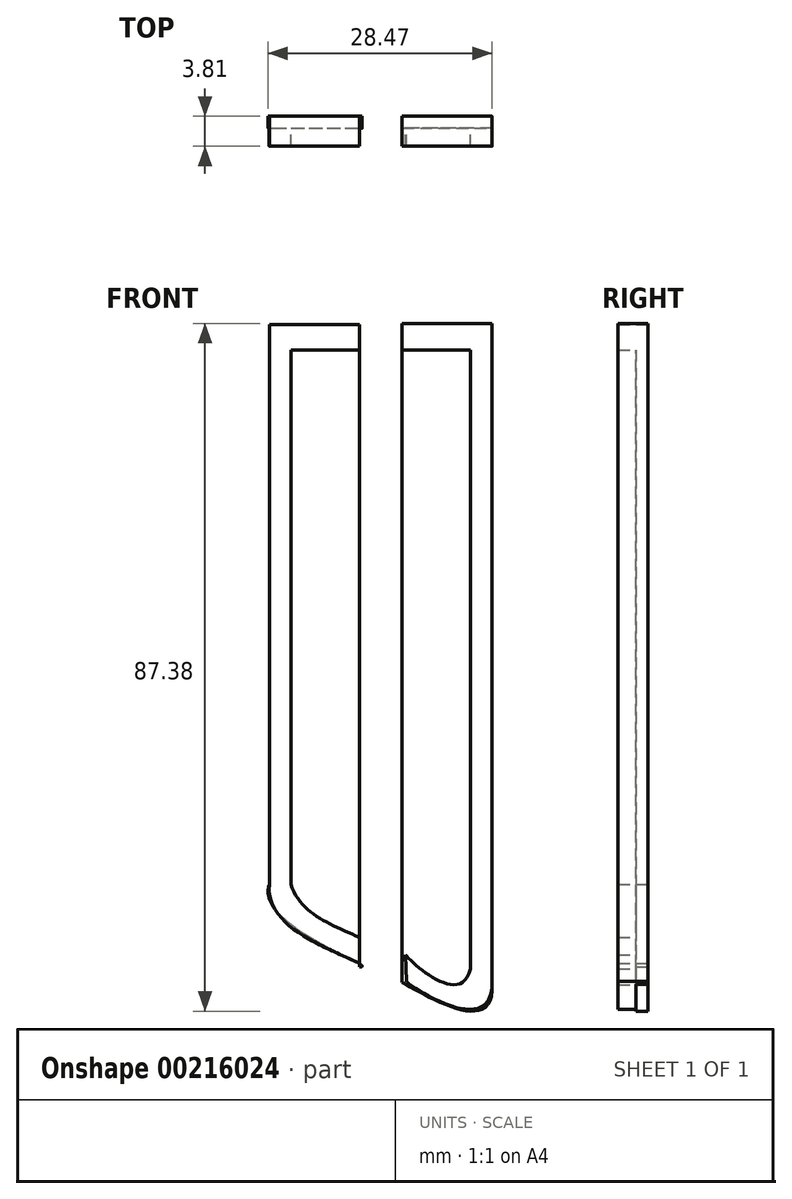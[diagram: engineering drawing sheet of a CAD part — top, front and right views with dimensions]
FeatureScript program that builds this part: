
annotation { "Feature Type Name" : "Feature", "Feature Type Description" : "" }
export const myFeature = defineFeature(function(context is Context, id is Id, definition is map)
    precondition{}
    {
        {
            var Q0;
            Q0=qCreatedBy(makeId("Front.planeOp"),FACE);
            var sketch = newSketch(context, id + "F0", { "sketchPlane" : qUnion([Q0])});
            skLineSegment(sketch, "E0", {"start": v(2.47, 36.27) * mm, "end": v(13.89, 36.27) * mm});
            skLineSegment(sketch, "E1", {"start": v(13.89, 36.27) * mm, "end": v(13.89, -47.55) * mm});
            skLineSegment(sketch, "E2", {"start": v(-2.98, 36.27) * mm, "end": v(-14.4, 36.27) * mm});
            skLineSegment(sketch, "E3", {"start": v(-14.4, 36.27) * mm, "end": v(-14.4, -34.85) * mm});
            skFitSpline(sketch, "E4", {"points": [v(-14.4, -34.85) * mm, v(-2.98, -45.36) * mm], "startDerivative": vector(-5.84, -16.35) * mm, "endDerivative": vector(-8.93, 0) * mm});
            skFitSpline(sketch, "E5", {"points": [v(2.47, -47.3) * mm, v(13.89, -47.55) * mm], "startDerivative": vector(10.51, -5.84) * mm, "endDerivative": vector(-1.1, 20.43) * mm});
            skLineSegment(sketch, "E6", {"start": v(-2.98, 36.27) * mm, "end": v(-2.98, -45.36) * mm});
            skLineSegment(sketch, "E7", {"start": v(2.47, 36.27) * mm, "end": v(2.47, -47.3) * mm});
            skSolve(sketch);
        }
        {
            var Q0;
            Q0 = qSketchRegion(id + "F0", true);
            extrude(context, id + "F1", {"entities" : qUnion([Q0]), "depth" : 1.52 * mm});
        }
        {
            var Q0;
            Q0=qCreatedBy(makeId("Front.planeOp"),FACE);
            var sketch = newSketch(context, id + "F2", { "sketchPlane" : qUnion([Q0])});
            skLineSegment(sketch, "E8", {"start": v(2.47, 36.4) * mm, "end": v(13.89, 36.4) * mm});
            skLineSegment(sketch, "E9", {"start": v(2.47, 36.4) * mm, "end": v(2.47, 33.03) * mm});
            skLineSegment(sketch, "E10", {"start": v(13.89, 36.4) * mm, "end": v(13.89, -47.18) * mm});
            skLineSegment(sketch, "E11", {"start": v(2.47, 33.03) * mm, "end": v(11.16, 33.03) * mm});
            skLineSegment(sketch, "E12", {"start": v(11.16, 33.03) * mm, "end": v(11.16, -45.62) * mm});
            skLineSegment(sketch, "E13", {"start": v(-2.86, 33.03) * mm, "end": v(-11.03, 33.03) * mm});
            skLineSegment(sketch, "E14", {"start": v(-3.11, 36.4) * mm, "end": v(-14.54, 36.4) * mm});
            skLineSegment(sketch, "E15", {"start": v(-14.54, 36.4) * mm, "end": v(-14.54, 33.03) * mm});
            skLineSegment(sketch, "E16", {"start": v(-14.54, 33.03) * mm, "end": v(-14.54, -34.85) * mm});
            skLineSegment(sketch, "E17", {"start": v(-11.03, 33.03) * mm, "end": v(-11.03, -32.9) * mm});
            skFitSpline(sketch, "E18", {"points": [v(11.16, -45.62) * mm, v(2.86, -43.8) * mm], "startDerivative": vector(-3.9, -14.4) * mm, "endDerivative": vector(-3.9, 4.28) * mm});
            skFitSpline(sketch, "E19", {"points": [v(13.89, -47.18) * mm, v(2.98, -47.18) * mm], "startDerivative": vector(0.78, -24.14) * mm, "endDerivative": vector(1.56, 0) * mm});
            skLineSegment(sketch, "E20", {"start": v(2.86, -43.8) * mm, "end": v(2.98, -47.18) * mm});
            skFitSpline(sketch, "E21", {"points": [v(-11.03, -32.9) * mm, v(-3.24, -40.69) * mm], "startDerivative": vector(0.39, -13.24) * mm, "endDerivative": vector(13.24, -6.62) * mm});
            skFitSpline(sketch, "E22", {"points": [v(-14.54, -34.85) * mm, v(-3.24, -44.97) * mm], "startDerivative": vector(-1.95, -15.18) * mm, "endDerivative": vector(11.3, -6.62) * mm});
            skLineSegment(sketch, "E23", {"start": v(-3.24, -40.69) * mm, "end": v(-3.24, -44.97) * mm});
            skSolve(sketch);
        }
        {
            var Q0;
            Q0 = qSketchRegion(id + "F2", true);
            extrude(context, id + "F3", {"entities" : qUnion([Q0]), "operationType" : NewBodyOperationType.ADD, "depth" : 3.8 * mm});
        }
        {
            var Q0;
            Q0=makeQuery(id+"F1.opExtrude","CAP_FACE",FACE,{"disambiguationData":[OSD([sQuery(id+"F0.wireOp",EDGE,"E2"),sQuery(id+"F0.wireOp",EDGE,"E3"),sQuery(id+"F0.wireOp",EDGE,"E4"),sQuery(id+"F0.wireOp",EDGE,"E6")])],"isStart":false});
            var sketch = newSketch(context, id + "F4", { "sketchPlane" : qUnion([Q0])});
            skLineSegment(sketch, "E24", {"start": v(-14.4, 36.27) * mm, "end": v(-2.98, 36.27) * mm});
            skLineSegment(sketch, "E25", {"start": v(-2.98, 36.27) * mm, "end": v(-14.4, 36.27) * mm});
            skLineSegment(sketch, "E26", {"start": v(-14.4, -34.85) * mm, "end": v(-14.4, 36.27) * mm});
            skLineSegment(sketch, "E27", {"start": v(-2.98, 36.27) * mm, "end": v(-2.98, 33.03) * mm});
            skLineSegment(sketch, "E28", {"start": v(-11.68, 33.03) * mm, "end": v(-2.98, 33.03) * mm});
            skLineSegment(sketch, "E29", {"start": v(-11.68, 33.03) * mm, "end": v(-11.68, -34.85) * mm});
            skFitSpline(sketch, "E30", {"points": [v(-14.4, -34.85) * mm, v(-2.98, -44.93) * mm], "startDerivative": vector(-1.56, -16.74) * mm, "endDerivative": vector(12.1, -6.23) * mm});
            skFitSpline(sketch, "E31", {"points": [v(-11.68, -34.85) * mm, v(-2.98, -41.6) * mm], "startDerivative": vector(3.9, -11.68) * mm, "endDerivative": vector(10.93, -5.06) * mm});
            skLineSegment(sketch, "E32", {"start": v(-2.98, -41.6) * mm, "end": v(-2.98, -44.93) * mm});
            skSolve(sketch);
        }
        {
            var Q0;
            Q0 = qSketchRegion(id + "F4", true);
            extrude(context, id + "F5", {"entities" : qUnion([Q0]), "operationType" : NewBodyOperationType.ADD, "depth" : 2.3 * mm});
        }
    });
